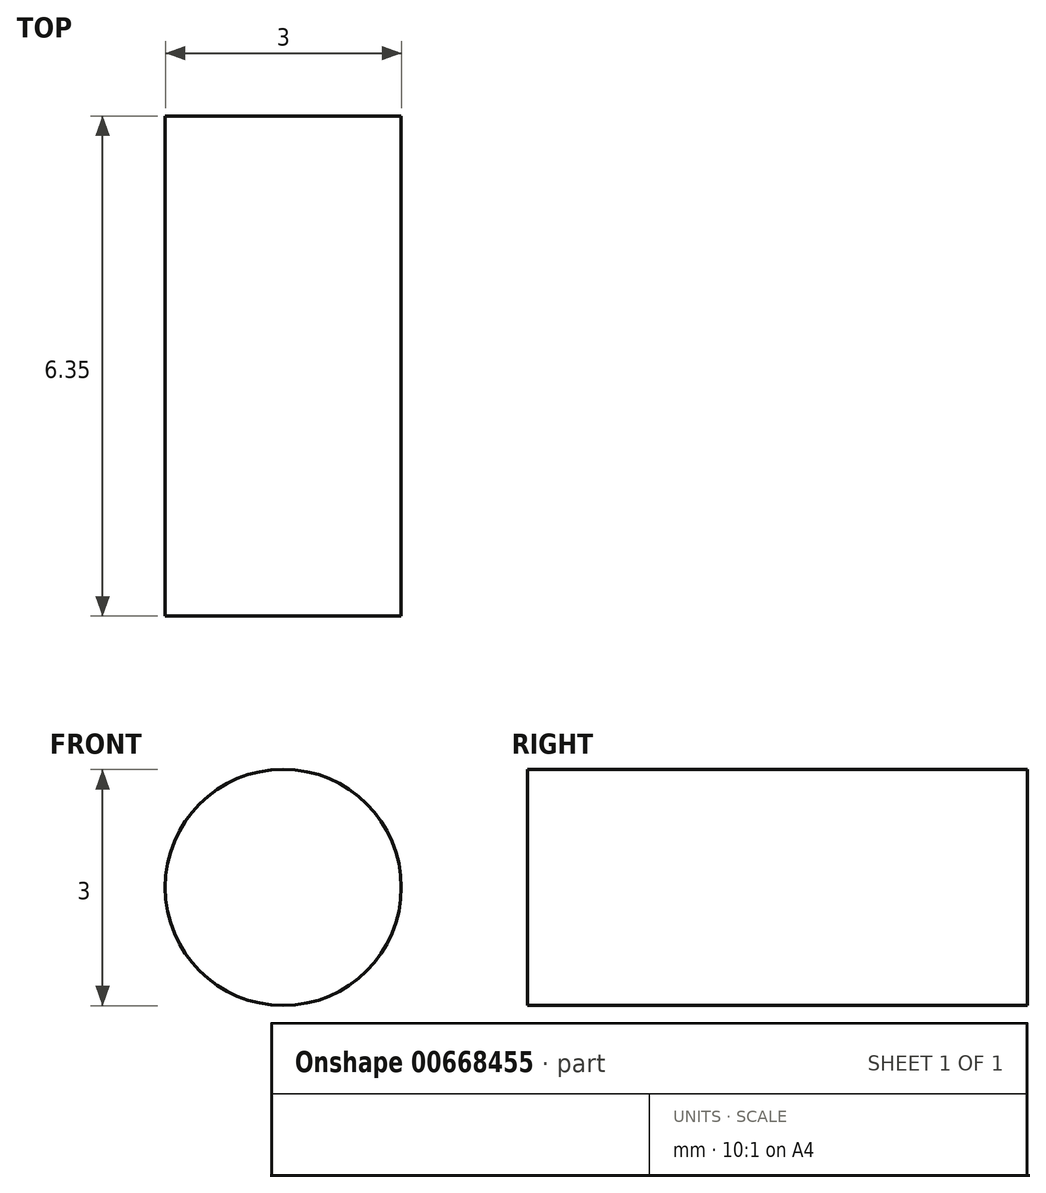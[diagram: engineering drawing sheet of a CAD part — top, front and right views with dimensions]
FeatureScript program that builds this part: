
annotation { "Feature Type Name" : "Feature", "Feature Type Description" : "" }
export const myFeature = defineFeature(function(context is Context, id is Id, definition is map)
    precondition{}
    {
        {
            var Q0;
            Q0=qCreatedBy(makeId("Front.planeOp"),FACE);
            var sketch = newSketch(context, id + "F0", { "sketchPlane" : qUnion([Q0])});
            skCircle(sketch, "E0", {"center": v(-39.3, 30.34) * mm, "radius": 1.5 * mm});
            skSolve(sketch);
        }
        {
            var Q0;
            Q0=makeQuery(id+"F0.imprint","IMPRINT",FACE,{"disambiguationData":[TD([[makeQuery(id+"F0.imprint","IMPRINT",EDGE,{"derivedFrom":sQuery(id+"F0.wireOp",EDGE,"E0")}),1.0]])]});
            extrude(context, id + "F1", {"entities" : qUnion([Q0]), "depth" : 6.35 * mm});
        }
    });
